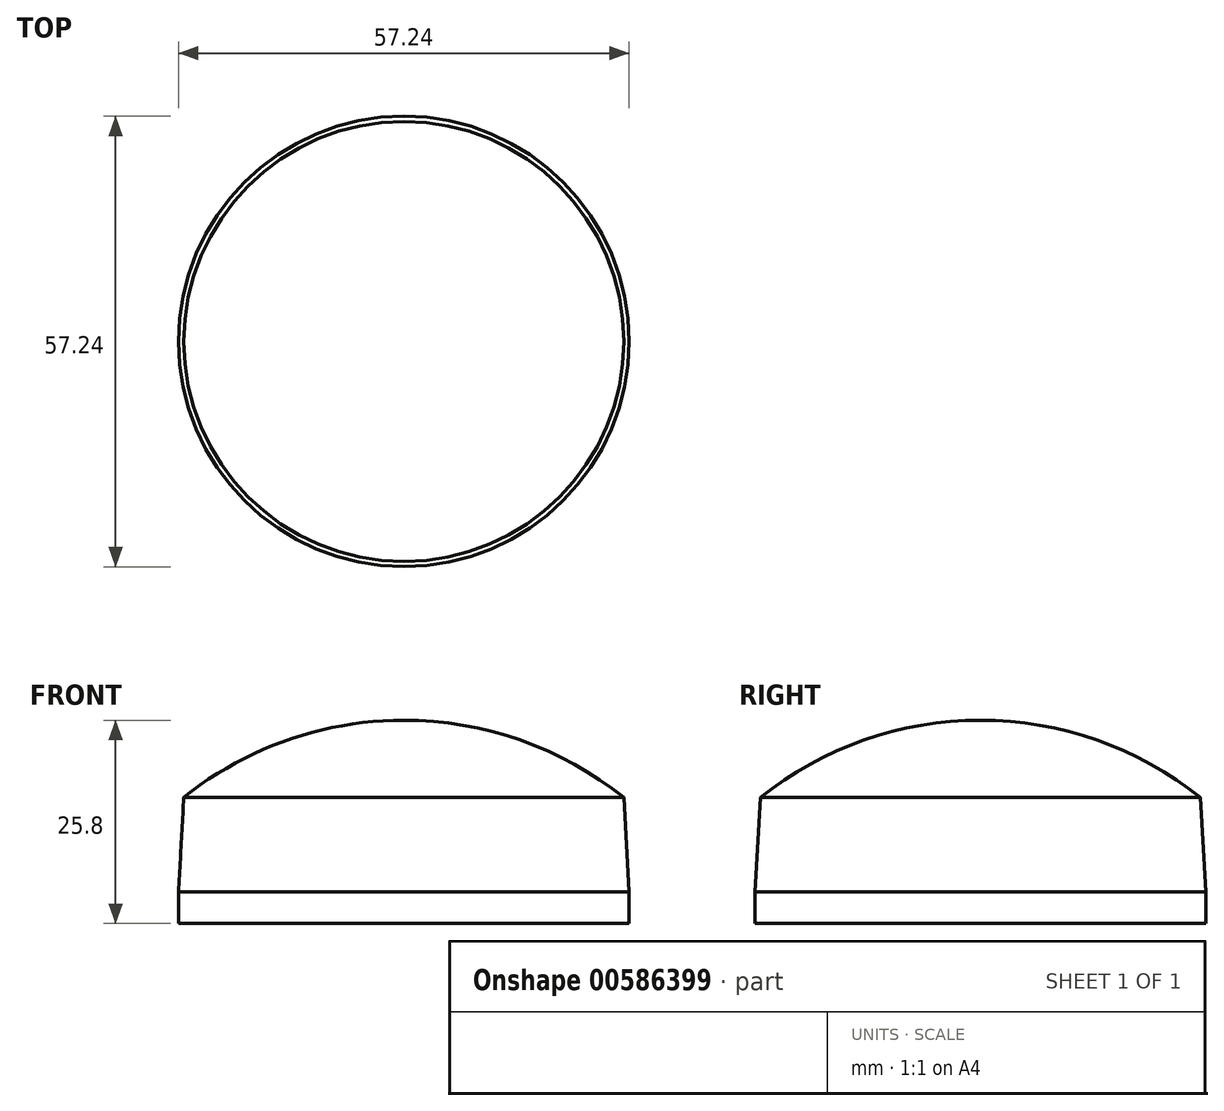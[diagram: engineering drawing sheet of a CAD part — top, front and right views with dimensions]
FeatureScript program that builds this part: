
annotation { "Feature Type Name" : "Feature", "Feature Type Description" : "" }
export const myFeature = defineFeature(function(context is Context, id is Id, definition is map)
    precondition{}
    {
        {
            var Q0;
            Q0=qCreatedBy(makeId("Front.planeOp"),FACE);
            var sketch = newSketch(context, id + "F0", { "sketchPlane" : qUnion([Q0])});
            skLineSegment(sketch, "E0", {"start": v(0, 0) * mm, "end": v(-27.95, 0) * mm, "construction": true});
            skLineSegment(sketch, "E1", {"start": v(0, 0) * mm, "end": v(0, -9) * mm});
            skLineSegment(sketch, "E2", {"start": v(0, 0) * mm, "end": v(0, 9.8) * mm});
            skLineSegment(sketch, "E3", {"start": v(0, -9) * mm, "end": v(-28.45, -9) * mm, "construction": true});
            skLineSegment(sketch, "E4", {"start": v(-27.95, 0) * mm, "end": v(-28.45, -9) * mm});
            skArc(sketch, "E5", {"start": v(0, 9.8) * mm, "mid": v(-14.8, 7.28) * mm, "end": v(-27.95, 0) * mm});
            skLineSegment(sketch, "E6", {"start": v(-27.95, 0) * mm, "end": v(-28.62, -12) * mm});
            skLineSegment(sketch, "E7", {"start": v(0, -9) * mm, "end": v(0, -12) * mm});
            skLineSegment(sketch, "E8", {"start": v(0, -12) * mm, "end": v(-28.62, -12) * mm, "construction": true});
            skLineSegment(sketch, "E9", {"start": v(-28.62, -12) * mm, "end": v(-28.62, -16) * mm});
            skLineSegment(sketch, "E10", {"start": v(0, -12) * mm, "end": v(0, -16) * mm});
            skLineSegment(sketch, "E11", {"start": v(0, -16) * mm, "end": v(-28.62, -16) * mm});
            skLineSegment(sketch, "E12", {"start": v(0, 9.8) * mm, "end": v(0, -16) * mm});
            skSolve(sketch);
        }
        {
            var Q0;
            {var subQ2=sQuery(id+"F0.wireOp",EDGE,"E5");Q0=makeQuery(id+"F0.imprint","IMPRINT",FACE,{"disambiguationData":[TD([[makeQuery(id+"F0.imprint","IMPRINT",EDGE,{"derivedFrom":subQ2}),1.0]])]});}
            var Q1;
            Q1=sQuery(id+"F0.wireOp",EDGE,"E5");
            var Q2;
            Q2=sQuery(id+"F0.wireOp",EDGE,"E2");
            var Q3;
            Q3=sQuery(id+"F0.wireOp",EDGE,"E1");
            var Q4;
            Q4=sQuery(id+"F0.wireOp",EDGE,"E3");
            var Q5;
            Q5=sQuery(id+"F0.wireOp",EDGE,"E4");
            var Q6;
            Q6=sQuery(id+"F0.wireOp",EDGE,"E2");
            revolve(context, id + "F1", {"entities" : qUnion([Q0]), "surfaceEntities" : qUnion([Q1, Q2, Q3, Q4, Q5]), "axis" : qUnion([Q6]), "revolveType" : RevolveType.FULL});
        }
    });
